# Revit family: HL_Стиральная устройство_HL406E
name_source: partatom
category: Instalační zařizovací předměty
revit_build: Autodesk Revit 2016 (Build: 20160525_1230(x64)
units: mm (PartAtom-declared; Revit-internal decimal feet)

## family parameters
Bod výpočtu místnosti = Ne
Hostitel = Plocha
Kóta kulaté spojky = Použít průměr
Nadpis OmniClass = Valves for Removal Systems
Ořezat dutým tvarem při načtení = Ne
Sdílené = Ne
Typ součásti = Normální
Číslo OmniClass = 23.70.50.21.37

## types (1)
- HL406E
    EAN = 9003076504077
    Klíčová poznámka = HL406E
    Komentáře k typům = Встроенный сифон для стиральной или посудомоечной машины DN40/50 с интегрированным подключением воды (настенная пластина впускное отверстие/выпускное отверсие R 1/2" внутренняя резьба), с водопроводным краном R 1/2" с предохранительным затвором обратного потока воды, с электрической розеткой (230V), со снимаемым корпусом оболочки, пластиной для монтажа, соединительным коленом 3/4" HL19.C и декоративной плитой из нержавеющей стали 100 х 280 мм. Монтаж : 75мм.
    Model = HL406E
    Popis = Стиральная устройство
    URL = http://www.hutterer-lechner.com
    Výchozí výška = 600 mm
    Výrobce = HL Hutterer & Lechner GmbH
    ВЕС = 1,31 [kg]
    ГЛУБИНА МОНТАЖА = 75-120 mm
    МАТЕРИАЛ = PE/ V2A
    ПРОИЗВОДИТЕЛЬНОСТЬ = 0,38 l/s
    РАЗМЕР = DN40/50

## geometry (parser evidence)
native form markers: Sweep x16
no freeform markers — native parametric forms only
